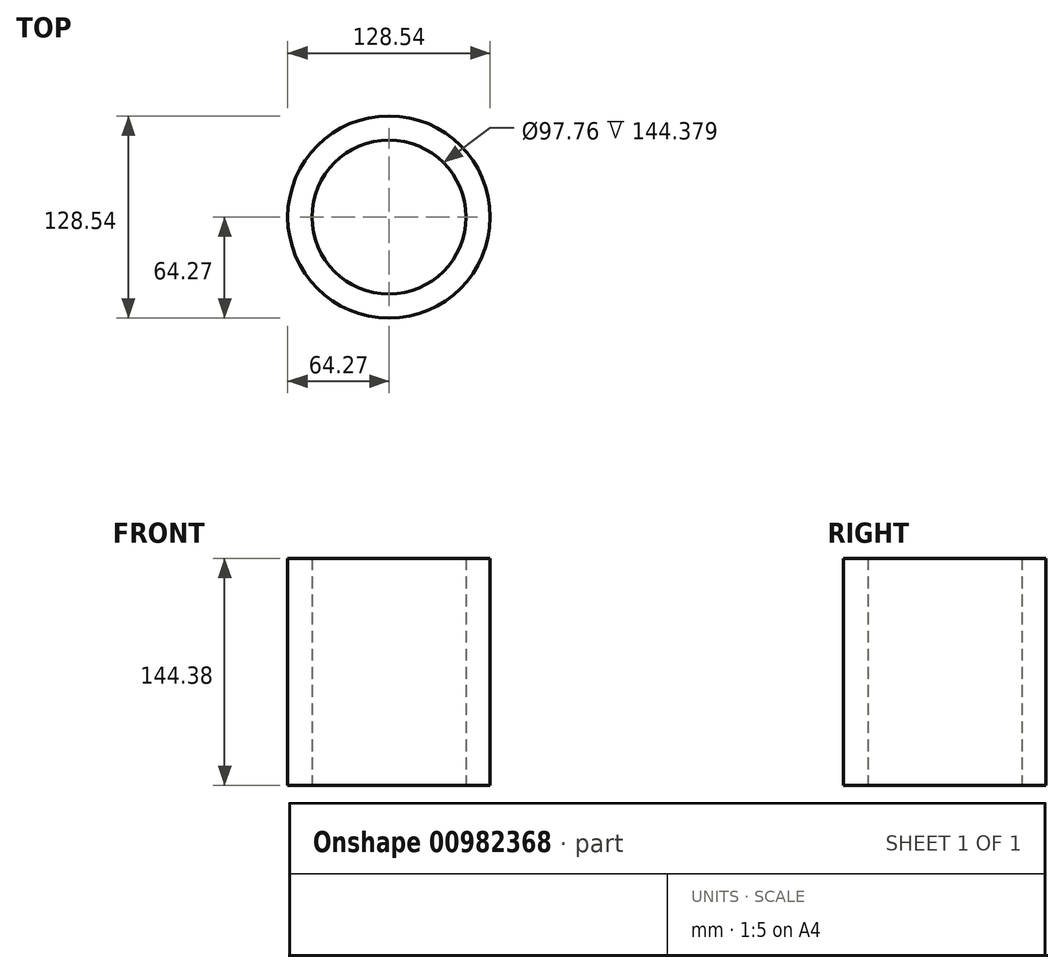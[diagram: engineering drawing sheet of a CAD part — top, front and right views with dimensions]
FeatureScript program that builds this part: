
annotation { "Feature Type Name" : "Feature", "Feature Type Description" : "" }
export const myFeature = defineFeature(function(context is Context, id is Id, definition is map)
    precondition{}
    {
        {
            var Q0;
            Q0=qCreatedBy(makeId("Top.planeOp"),FACE);
            var sketch = newSketch(context, id + "F0", { "sketchPlane" : qUnion([Q0])});
            skCircle(sketch, "E0", {"center": v(0, 0) * mm, "radius": 48.88 * mm});
            skCircle(sketch, "E1", {"center": v(0, 0) * mm, "radius": 64.27 * mm});
            skSolve(sketch);
        }
        {
            var Q0;
            Q0 = qSketchRegion(id + "F0", true);
            extrude(context, id + "F1", {"entities" : qUnion([Q0]), "depth" : 144.38 * mm, "offsetDistance" : 25.4 * mm});
        }
    });
